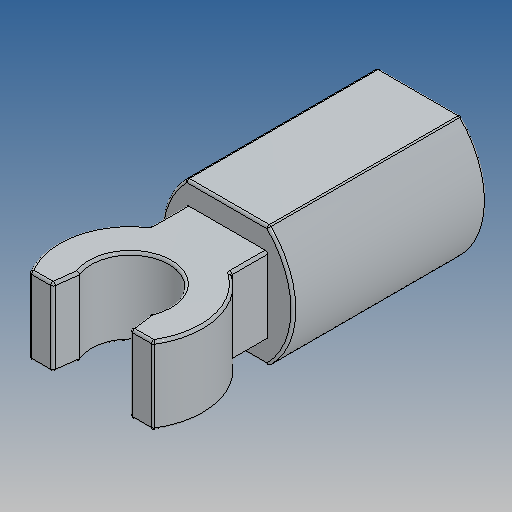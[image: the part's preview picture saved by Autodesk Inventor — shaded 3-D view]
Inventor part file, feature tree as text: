
AUTODESK INVENTOR PART (.ipt)
format: ipt  version: 2025 (Build 290162010, 162A)  size: 217,600 bytes
history: native  units: in
note: dims shown in document units (in); Inventor stores cm internally (conversion verified against a paired STEP export)
features: extrude x3, sketch x2, fillet x1
ambient origin geometry x8: Origin, YZ Plane, XZ Plane, XY Plane, X Axis, Y Axis, Z Axis, Center Point
bodies: Solid1 (feature_tree)
feature tree (6):
  sketch  "Sketch2"  dims[d0=0.1969in d2=0.126in]
  extrude  "Extrusion1"  Depth=0.126in
  extrude  "Extrusion2"  TaperAngle=0.0deg  [1 undecoded]
  extrude  "Extrusion3"  Depth=0.1575in
  fillet  "Fillet1"  [1 undecoded]
  sketch  "Sketch3"  dims[d3=0.315in d4=0.0in d5=0.1575in d6=0.0in d7=0.1335in d9=0.2161in d10=0.126in d11=0.1161in d12=0.126in d13=0.2205in d14=0.1575in d16=0.132in d17=0.2362in d18=0.126in d19=0.0in d20=0.0039in]
note: 2 required parameter values undecoded (feature->parameter linkage not recoverable at this tier; creation-order binding heuristic only, values carry confidence <= 0.55)
